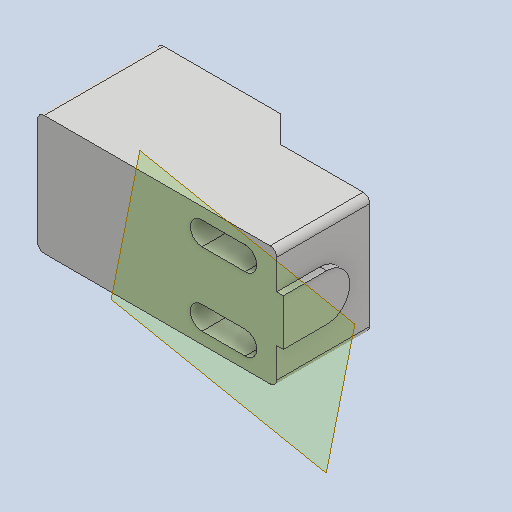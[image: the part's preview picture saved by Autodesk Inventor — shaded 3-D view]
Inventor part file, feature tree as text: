
AUTODESK INVENTOR PART (.ipt)
format: ipt  version: 2023 (Build 270158000, 158)  size: 161,792 bytes
history: native  units: mm
features: other x4, plane x1
ambient origin geometry x8: Origin, YZ Plane, XZ Plane, XY Plane, X Axis, Y Axis, Z Axis, Center Point
bodies: Solid1 (feature_tree)
feature tree (5):
  plane  "Work Plane1"
  other  "Âûðåç-Âûòÿíóòü3"
  other  "<userpath>\OneDrive\Objet3D\3DPrinter\3DPrinterBeltCoreXY.iam"
  other  "3DPrinterBeltCoreXY.iam"
  other  "HotendMountCarriage:1"
